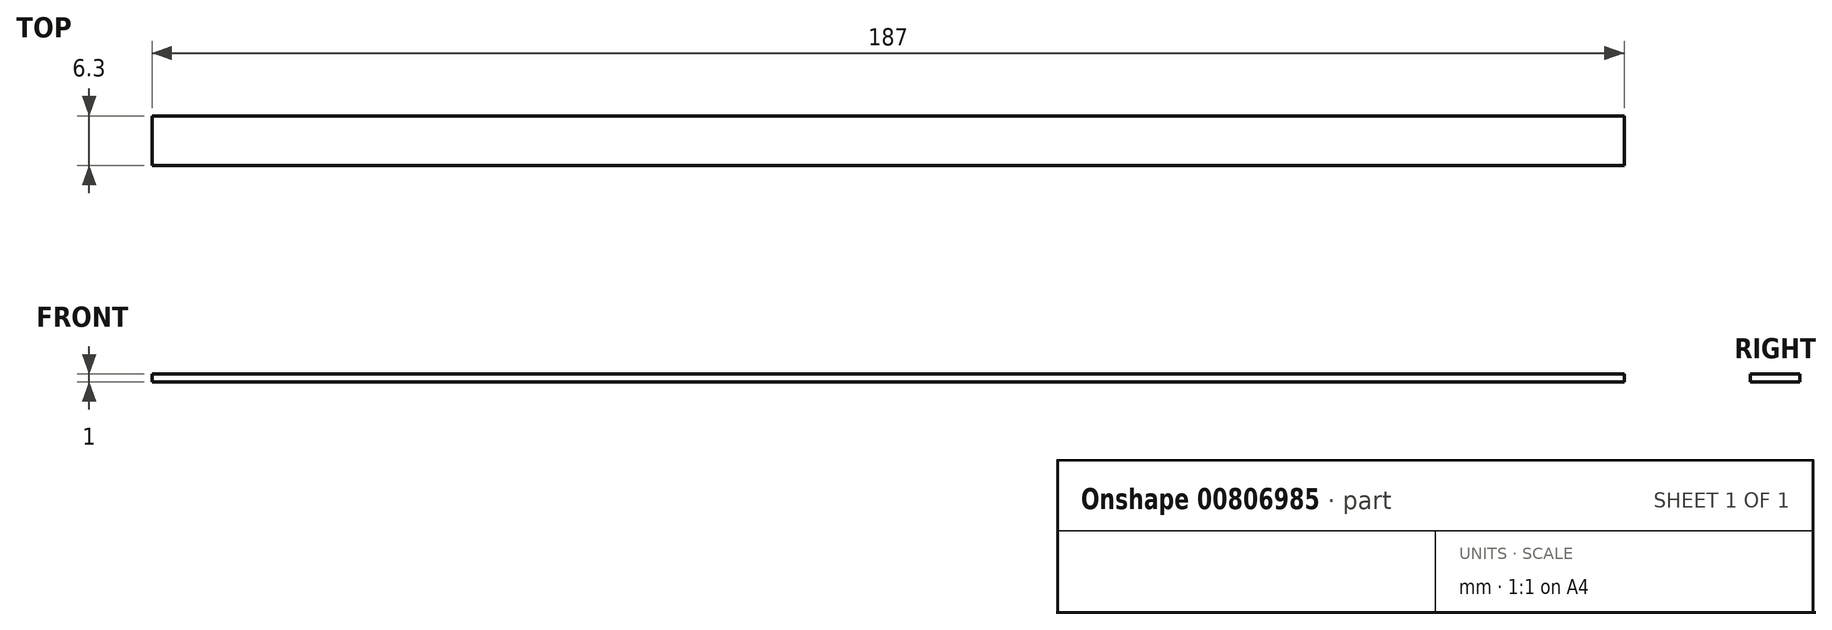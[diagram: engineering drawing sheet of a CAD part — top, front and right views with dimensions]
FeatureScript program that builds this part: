
annotation { "Feature Type Name" : "Feature", "Feature Type Description" : "" }
export const myFeature = defineFeature(function(context is Context, id is Id, definition is map)
    precondition{}
    {
        {
            var Q0;
            Q0=qCreatedBy(makeId("Top.planeOp"),FACE);
            var sketch = newSketch(context, id + "F0", { "sketchPlane" : qUnion([Q0])});
            skLineSegment(sketch, "E0.bottom", {"start": v(-93.5, 3.15) * mm, "end": v(93.5, 3.15) * mm});
            skLineSegment(sketch, "E0.top", {"start": v(-93.5, -3.15) * mm, "end": v(93.5, -3.15) * mm});
            skLineSegment(sketch, "E0.left", {"start": v(-93.5, 3.15) * mm, "end": v(-93.5, -3.15) * mm});
            skLineSegment(sketch, "E0.right", {"start": v(93.5, 3.15) * mm, "end": v(93.5, -3.15) * mm});
            skSolve(sketch);
        }
        {
            var Q0;
            Q0=makeQuery(id+"F0.imprint","IMPRINT",FACE,{"disambiguationData":[TD([[makeQuery(id+"F0.imprint","IMPRINT",EDGE,{"derivedFrom":sQuery(id+"F0.wireOp",EDGE,"E0.bottom")}),-1.0]])]});
            extrude(context, id + "F1", {"entities" : qUnion([Q0]), "depth" : 1 * mm, "offsetDistance" : 25 * mm});
        }
    });
